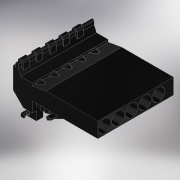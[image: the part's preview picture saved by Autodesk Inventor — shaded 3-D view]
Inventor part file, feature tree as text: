
AUTODESK INVENTOR PART (.ipt)
format: ipt  version: 2018 (Build 220112000, 112)  size: 747,520 bytes
history: native  units: in
note: dims shown in document units (in); Inventor stores cm internally (conversion verified against a paired STEP export)
features: extrude x17, other x15, fillet x3, sketch x3, projected_geometry x3, chamfer x2, pattern_linear x1
ambient origin geometry x8: Origin, YZ Plane, XZ Plane, XY Plane, X Axis, Y Axis, Z Axis, Center Point
bodies: Solid1 (feature_tree)
feature tree (44):
  other  "Base Sketch"
  extrude  "Side Walls"  TaperAngle=0.0deg  [1 undecoded]
  extrude  "Back Wall"  TaperAngle=0.0deg  [1 undecoded]
  extrude  "Front Wall"  Depth=0.0157in
  extrude  "Whistle Housing"  Depth=0.0157in
  extrude  "Tube Socket"  Depth=0.0157in
  other  "Midplane"
  extrude  "Slit"  Depth=0.0157in
  other  "Silicone Fitting"
  extrude  "Silicone Fitting to Chamber"  TaperAngle=90.0deg  [1 undecoded]
  extrude  "Hinge"  Depth=0.0157in TaperAngle=0.0deg
  extrude  "Hinge Nub"  Depth=0.3937in
  chamfer  "Hinge Clearance Chamfer"  [1 undecoded]
  chamfer  "Spring Pass Chamfer"  Distance=0.4331in
  extrude  "Spring Block"  Depth=0.4134in
  extrude  "Spring Hook"  TaperAngle=0.0deg  [1 undecoded]
  other  "Sping Hook Draft"
  fillet  "Spring Hook Fillet"  Radius=0.189in
  extrude  "Edge Cut"  TaperAngle=0.0deg  [1 undecoded]
  fillet  "Edge Fillet"  Radius=0.0079in
  other  "Pincher Triangle Sketch"
  extrude  "Pincher Triangle"  Depth=0.0787in
  extrude  "Triangle Coupling Male"  TaperAngle=45.0deg  [1 undecoded]
  extrude  "Fill: Triangle Coupling Female"  Depth=0.0787in TaperAngle=45.0deg
  pattern_linear  "Key Repitition"  Spacing1=0.2067in  [1 undecoded]
  extrude  "Extrusion28"  Depth=0.0157in
  extrude  "Extrusion29"  Depth=0.0157in
  fillet  "Fillet20"  [1 undecoded]
  sketch  "Sketch5"  dims[d1=0.0in d2=0.0in]
  projected_geometry  "Projected Loop2"
  other  "Whistle Housing Sketch"
  other  "Edge Cut Sketch"
  other  "Slit Sketch"
  other  "Silicone Fitting Sketch"
  other  "Silicone Fitting to Chamber Sketch"
  other  "Tube Socket Sketch"
  other  "Hinge Sketch"
  other  "Hinge Nub Sketch"
  other  "Spring Block Sketch"
  other  "Spring Hook Sketch"
  sketch  "Sketch28"  dims[d3=0.0in d4=0.0in]
  projected_geometry  "Projected Loop4"
  sketch  "Sketch29"  dims[d61=1.5748in d62=0.0in d65=0.0938in d66=0.1181in d67=0.0276in d68=0.0197in d69=90.0deg d71=1.5748in d72=0.0in d78=0.3937in d80=0.0in d81=0.4331in d88=0.4134in d89=0.0in d92=0.189in d93=0.0in d101=0.0079in d105=0.0787in d106=0.1772in d107=45.0deg d112=0.0787in d113=45.0deg d135=0.2067in d136=0.315in d137=0.5906in d139=0.0in d160=0.1181in d161=0.0984in d162=0.3937in d163=0.1575in d164=0.0in d171=1.03in d173=0.4724in d176=0.4134in d177=0.0in d178=0.2067in d179=0.0in d180=0.1374in d181=0.0394in d187=0.2067in d188=0.2362in d190=0.5906in d191=0.0in d193=0.1654in d194=0.0512in d198=0.4134in d199=0.0in d277=0.0079in d278=1.9685in d280=0.4134in d282=0.4134in d283=0.0in d284=0.0394in d285=0.0079in d289=0.0827in d298=0.2067in d299=0.0in d300=0.2559in d301=0.0in d302=0.1969in d303=0.0in d304=0.0787in d305=0.315in d306=0.0079in d307=0.0394in d308=0.0157in]
  projected_geometry  "Projected Loop5"
note: 9 required parameter values undecoded (feature->parameter linkage not recoverable at this tier; creation-order binding heuristic only, values carry confidence <= 0.55)
